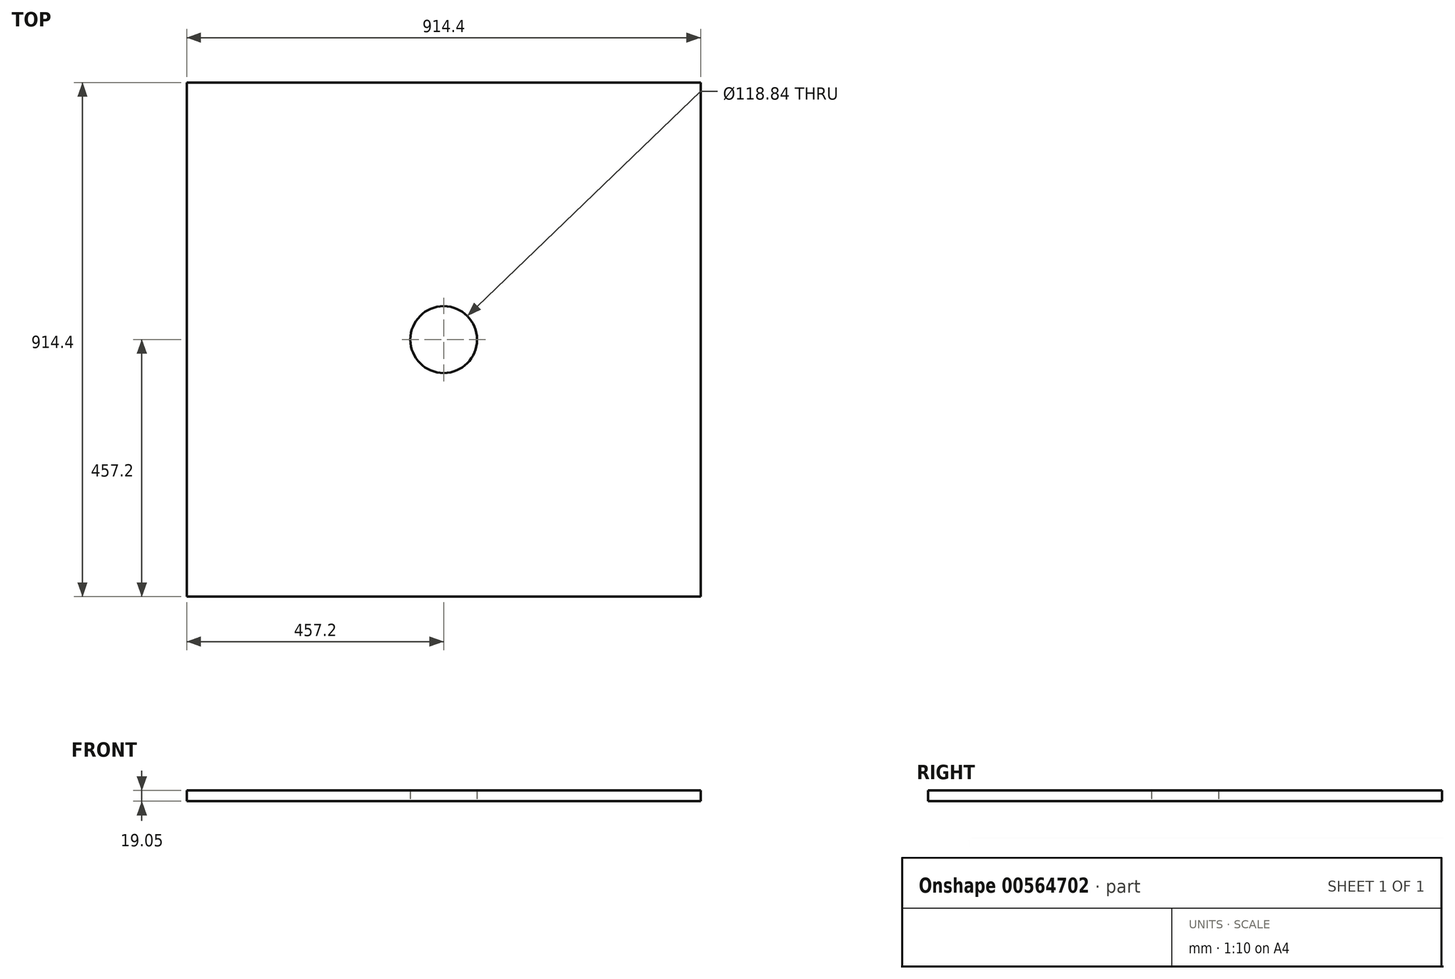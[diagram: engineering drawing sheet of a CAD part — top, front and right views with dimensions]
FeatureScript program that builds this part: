
annotation { "Feature Type Name" : "Feature", "Feature Type Description" : "" }
export const myFeature = defineFeature(function(context is Context, id is Id, definition is map)
    precondition{}
    {
        {
            var Q0;
            Q0=qCreatedBy(makeId("Top.planeOp"),FACE);
            var sketch = newSketch(context, id + "F0", { "sketchPlane" : qUnion([Q0])});
            skLineSegment(sketch, "E0.bottom", {"start": v(457.2, 457.2) * mm, "end": v(-457.2, 457.2) * mm});
            skLineSegment(sketch, "E0.top", {"start": v(457.2, -457.2) * mm, "end": v(-457.2, -457.2) * mm});
            skLineSegment(sketch, "E0.left", {"start": v(457.2, 457.2) * mm, "end": v(457.2, -457.2) * mm});
            skLineSegment(sketch, "E0.right", {"start": v(-457.2, 457.2) * mm, "end": v(-457.2, -457.2) * mm});
            skPoint(sketch, "E0.middle", {"position": v(0, 0) * mm});
            skCircle(sketch, "E1", {"center": v(0, 0) * mm, "radius": 59.42 * mm});
            skSolve(sketch);
        }
        {
            var Q0;
            Q0=makeQuery(id+"F0.imprint","IMPRINT",FACE,{"disambiguationData":[TD([[makeQuery(id+"F0.imprint","IMPRINT",EDGE,{"derivedFrom":sQuery(id+"F0.wireOp",EDGE,"E0.bottom")}),1.0]])]});
            extrude(context, id + "F1", {"entities" : qUnion([Q0]), "depth" : 19.05 * mm, "offsetDistance" : 25.4 * mm});
        }
    });
